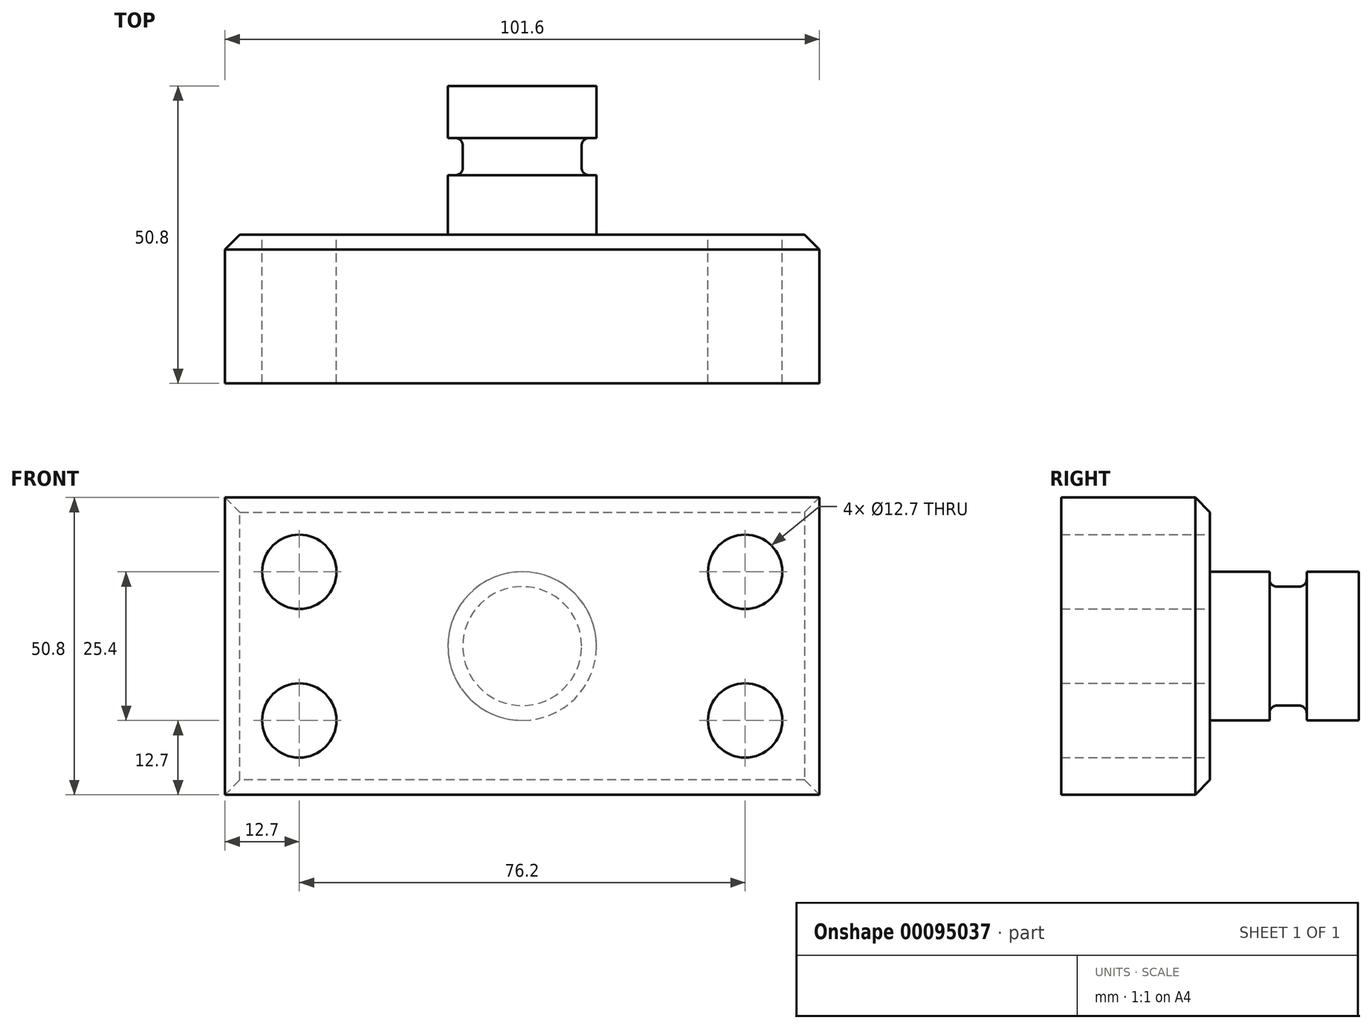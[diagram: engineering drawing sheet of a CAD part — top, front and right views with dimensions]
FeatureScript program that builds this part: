
annotation { "Feature Type Name" : "Feature", "Feature Type Description" : "" }
export const myFeature = defineFeature(function(context is Context, id is Id, definition is map)
    precondition{}
    {
        {
            var Q0;
            Q0=qCreatedBy(makeId("Front.planeOp"),FACE);
            var sketch = newSketch(context, id + "F0", { "sketchPlane" : qUnion([Q0])});
            skLineSegment(sketch, "E0.bottom", {"start": v(-50.8, 25.4) * mm, "end": v(50.8, 25.4) * mm});
            skLineSegment(sketch, "E0.top", {"start": v(-50.8, -25.4) * mm, "end": v(50.8, -25.4) * mm});
            skLineSegment(sketch, "E0.left", {"start": v(-50.8, 25.4) * mm, "end": v(-50.8, -25.4) * mm});
            skLineSegment(sketch, "E0.right", {"start": v(50.8, 25.4) * mm, "end": v(50.8, -25.4) * mm});
            skPoint(sketch, "E0.middle", {"position": v(0, 0) * mm});
            skSolve(sketch);
        }
        {
            var Q0;
            Q0=makeQuery(id+"F0.imprint","IMPRINT",FACE,{"disambiguationData":[TD([[makeQuery(id+"F0.imprint","IMPRINT",EDGE,{"derivedFrom":sQuery(id+"F0.wireOp",EDGE,"E0.bottom")}),-1.0]])]});
            extrude(context, id + "F1", {"entities" : qUnion([Q0]), "oppositeDirection" : true, "depth" : 25.4 * mm});
        }
        {
            var Q0;
            Q0=makeQuery(id+"F1.opExtrude","CAP_FACE",FACE,{"disambiguationData":[OSD([sQuery(id+"F0.wireOp",EDGE,"E0.bottom"),sQuery(id+"F0.wireOp",EDGE,"E0.top"),sQuery(id+"F0.wireOp",EDGE,"E0.left"),sQuery(id+"F0.wireOp",EDGE,"E0.right")])],"isStart":false});
            var sketch = newSketch(context, id + "F2", { "sketchPlane" : qUnion([Q0])});
            skCircle(sketch, "E1", {"center": v(-38.1, 12.7) * mm, "radius": 6.35 * mm});
            skCircle(sketch, "E2", {"center": v(-38.1, -12.7) * mm, "radius": 6.35 * mm});
            skCircle(sketch, "E3", {"center": v(38.1, 12.7) * mm, "radius": 6.35 * mm});
            skCircle(sketch, "E4", {"center": v(38.1, -12.7) * mm, "radius": 6.35 * mm});
            skSolve(sketch);
        }
        {
            var Q0;
            Q0 = qSketchRegion(id + "F2", true);
            extrude(context, id + "F3", {"entities" : qUnion([Q0]), "operationType" : NewBodyOperationType.REMOVE, "endBound" : BoundingType.THROUGH_ALL, "oppositeDirection" : true, "depth" : 25.4 * mm});
        }
        {
            var Q0;
            Q0=qCreatedBy(makeId("Top.planeOp"),FACE);
            var sketch = newSketch(context, id + "F4", { "sketchPlane" : qUnion([Q0])});
            skLineSegment(sketch, "E5.bottom", {"start": v(0, 25.4) * mm, "end": v(-12.7, 25.4) * mm});
            skLineSegment(sketch, "E5.top", {"start": v(0, 50.8) * mm, "end": v(-12.7, 50.8) * mm});
            skLineSegment(sketch, "E5.left", {"start": v(0, 25.4) * mm, "end": v(0, 50.8) * mm});
            skLineSegment(sketch, "E5.right", {"start": v(-12.7, 25.4) * mm, "end": v(-12.7, 50.8) * mm});
            skSolve(sketch);
        }
        {
            var Q0;
            Q0 = qSketchRegion(id + "F4", true);
            var Q1;
            Q1=sQuery(id+"F4.wireOp",EDGE,"E5.left");
            revolve(context, id + "F5", {"operationType" : NewBodyOperationType.ADD, "entities" : qUnion([Q0]), "axis" : qUnion([Q1]), "revolveType" : RevolveType.FULL});
        }
        {
            var Q0;
            Q0=qCreatedBy(makeId("Top.planeOp"),FACE);
            var sketch = newSketch(context, id + "F6", { "sketchPlane" : qUnion([Q0])});
            skLineSegment(sketch, "E6.bottom", {"start": v(-10.16, 35.56) * mm, "end": v(-18.2, 35.56) * mm});
            skLineSegment(sketch, "E6.top", {"start": v(-10.16, 41.9) * mm, "end": v(-18.2, 41.9) * mm});
            skLineSegment(sketch, "E6.left", {"start": v(-10.16, 35.56) * mm, "end": v(-10.16, 41.9) * mm});
            skLineSegment(sketch, "E6.right", {"start": v(-18.2, 35.56) * mm, "end": v(-18.2, 41.9) * mm});
            skLineSegment(sketch, "E7", {"start": v(0, 0) * mm, "end": v(0, 68.07) * mm, "construction": true});
            skSolve(sketch);
        }
        {
            var Q0;
            Q0=makeQuery(id+"F6.imprint","IMPRINT",FACE,{"disambiguationData":[TD([[makeQuery(id+"F6.imprint","IMPRINT",EDGE,{"derivedFrom":sQuery(id+"F6.wireOp",EDGE,"E6.bottom")}),-1.0]])]});
            var Q1;
            Q1=sQuery(id+"F6.wireOp",EDGE,"E7");
            revolve(context, id + "F7", {"operationType" : NewBodyOperationType.REMOVE, "entities" : qUnion([Q0]), "axis" : qUnion([Q1]), "revolveType" : RevolveType.FULL, "oppositeDirection" : true});
        }
        {
            var Q0;
            Q0=makeQuery(id+"F5.opRevolve","SWEPT_EDGE",EDGE,{"disambiguationData":[OSD([sQuery(id+"F4.wireOp",EDGE,"E5.bottom"),sQuery(id+"F4.wireOp",EDGE,"E5.right")])]});
            var Q1;
            Q1=makeQuery(id+"F7.boolean.opBoolean","COPY",EDGE,{"derivedFrom":makeQuery(id+"F7.opRevolve","SWEPT_EDGE",EDGE,{"disambiguationData":[OSD([sQuery(id+"F6.wireOp",EDGE,"E6.bottom"),sQuery(id+"F6.wireOp",EDGE,"E6.left")])]})});
            var Q2;
            Q2=makeQuery(id+"F7.boolean.opBoolean","COPY",EDGE,{"derivedFrom":makeQuery(id+"F7.opRevolve","SWEPT_EDGE",EDGE,{"disambiguationData":[OSD([sQuery(id+"F6.wireOp",EDGE,"E6.top"),sQuery(id+"F6.wireOp",EDGE,"E6.left")])]})});
            fillet(context, id + "F8", {"entities" : qUnion([Q0, Q1, Q2]), "radius" : 1.27 * mm, "tangentPropagation" : true, "allowEdgeOverflow" : false});
        }
        {
            var Q0;
            Q0=makeQuery(id+"F1.opExtrude","CAP_EDGE",EDGE,{"disambiguationData":[OSD([sQuery(id+"F0.wireOp",EDGE,"E0.right")])],"isStart":false});
            var Q1;
            Q1=makeQuery(id+"F1.opExtrude","CAP_EDGE",EDGE,{"disambiguationData":[OSD([sQuery(id+"F0.wireOp",EDGE,"E0.bottom")])],"isStart":false});
            var Q2;
            Q2=makeQuery(id+"F1.opExtrude","CAP_EDGE",EDGE,{"disambiguationData":[OSD([sQuery(id+"F0.wireOp",EDGE,"E0.left")])],"isStart":false});
            var Q3;
            Q3=makeQuery(id+"F1.opExtrude","CAP_EDGE",EDGE,{"disambiguationData":[OSD([sQuery(id+"F0.wireOp",EDGE,"E0.top")])],"isStart":false});
            chamfer(context, id + "F9", {"entities" : qUnion([Q0, Q1, Q2, Q3]), "width" : 2.54 * mm, "tangentPropagation" : true});
        }
    });
